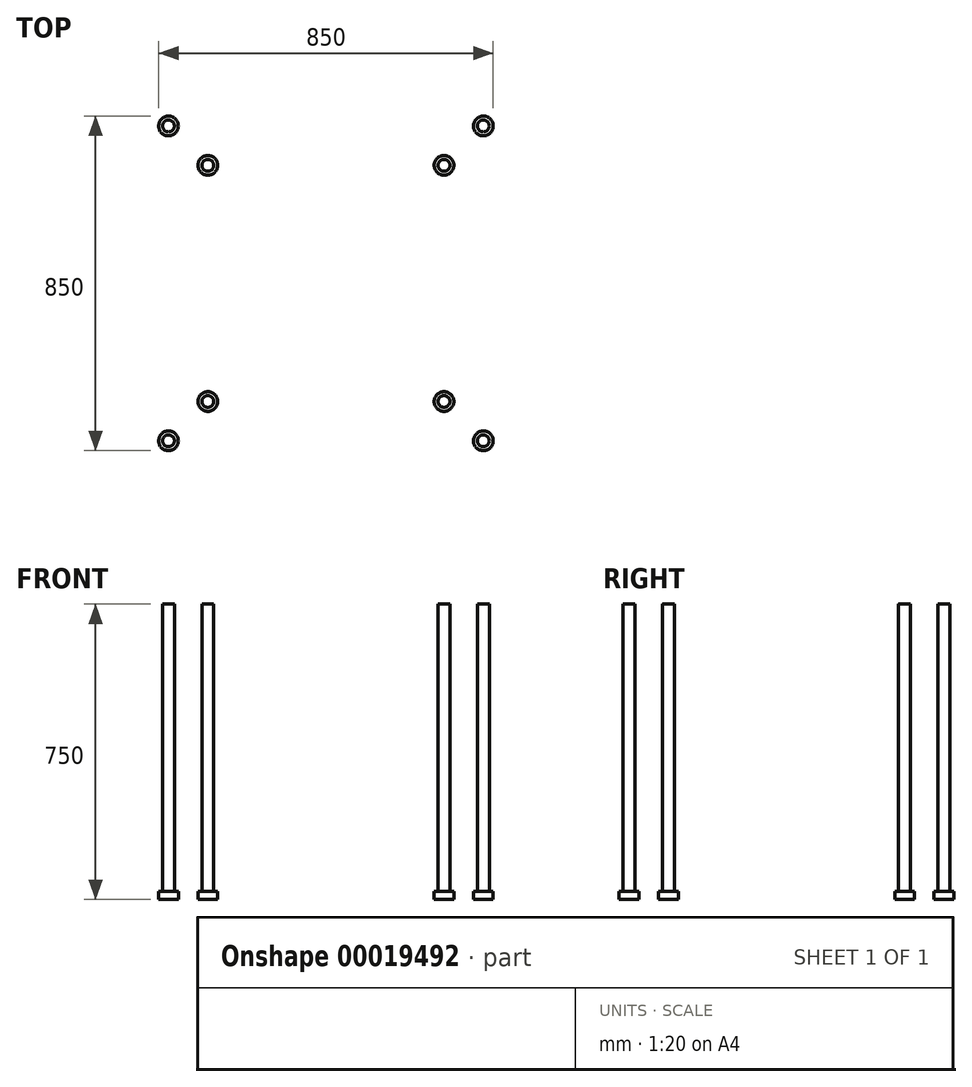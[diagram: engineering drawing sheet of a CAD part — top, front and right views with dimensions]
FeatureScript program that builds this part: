
annotation { "Feature Type Name" : "Feature", "Feature Type Description" : "" }
export const myFeature = defineFeature(function(context is Context, id is Id, definition is map)
    precondition{}
    {
        {
            var Q0;
            Q0=qCreatedBy(makeId("Top.planeOp"),FACE);
            var sketch = newSketch(context, id + "F0", { "sketchPlane" : qUnion([Q0])});
            skLineSegment(sketch, "E0.rect.bottom", {"start": v(300, -300) * mm, "end": v(-300, -300) * mm});
            skLineSegment(sketch, "E0.rect.top", {"start": v(300, 300) * mm, "end": v(-300, 300) * mm});
            skLineSegment(sketch, "E0.rect.left", {"start": v(300, -300) * mm, "end": v(300, 300) * mm});
            skLineSegment(sketch, "E0.rect.right", {"start": v(-300, -300) * mm, "end": v(-300, 300) * mm});
            skPoint(sketch, "E0.rect.middle", {"position": v(0, 0) * mm});
            skLineSegment(sketch, "E1.rect.bottom", {"start": v(400, -400) * mm, "end": v(-400, -400) * mm});
            skLineSegment(sketch, "E1.rect.top", {"start": v(400, 400) * mm, "end": v(-400, 400) * mm});
            skLineSegment(sketch, "E1.rect.left", {"start": v(400, -400) * mm, "end": v(400, 400) * mm});
            skLineSegment(sketch, "E1.rect.right", {"start": v(-400, -400) * mm, "end": v(-400, 400) * mm});
            skCircle(sketch, "E2", {"center": v(-400, -400) * mm, "radius": 25 * mm});
            skCircle(sketch, "E3", {"center": v(-300, -300) * mm, "radius": 25 * mm});
            skCircle(sketch, "E4", {"center": v(300, -300) * mm, "radius": 25 * mm});
            skCircle(sketch, "E5", {"center": v(400, -400) * mm, "radius": 25 * mm});
            skCircle(sketch, "E6", {"center": v(300, 300) * mm, "radius": 25 * mm});
            skCircle(sketch, "E7", {"center": v(400, 400) * mm, "radius": 25 * mm});
            skCircle(sketch, "E8", {"center": v(-400, 400) * mm, "radius": 25 * mm});
            skCircle(sketch, "E9", {"center": v(-300, 300) * mm, "radius": 25 * mm});
            skCircle(sketch, "E10", {"center": v(-400, 400) * mm, "radius": 15 * mm});
            skCircle(sketch, "E11", {"center": v(-300, 300) * mm, "radius": 15 * mm});
            skCircle(sketch, "E12", {"center": v(-400, -400) * mm, "radius": 15 * mm});
            skCircle(sketch, "E13", {"center": v(-300, -300) * mm, "radius": 15 * mm});
            skCircle(sketch, "E14", {"center": v(300, -300) * mm, "radius": 15 * mm});
            skCircle(sketch, "E15", {"center": v(400, -400) * mm, "radius": 15 * mm});
            skCircle(sketch, "E16", {"center": v(300, 300) * mm, "radius": 15 * mm});
            skCircle(sketch, "E17", {"center": v(400, 400) * mm, "radius": 15 * mm});
            skSolve(sketch);
        }
        {
            var Q0;
            {var subQ1=sQuery(id+"F0.wireOp",EDGE,"E1.rect.left");var subQ3=sQuery(id+"F0.wireOp",EDGE,"E1.rect.bottom");var subQ5=makeQuery(id+"F0.imprint","INTERSECT",VERTEX,{"derivedFrom":[subQ3,subQ1]});Q0=makeQuery(id+"F0.imprint","IMPRINT",FACE,{"disambiguationData":[TD([[makeQuery(id+"F0.imprint","IMPRINT",EDGE,{"disambiguationData":[TD([[subQ5,-1.0]])],"derivedFrom":subQ3}),1.0]])]});}
            var Q1;
            {var subQ1=sQuery(id+"F0.wireOp",EDGE,"E1.rect.left");var subQ3=sQuery(id+"F0.wireOp",EDGE,"E1.rect.bottom");var subQ5=makeQuery(id+"F0.imprint","INTERSECT",VERTEX,{"derivedFrom":[subQ3,subQ1]});Q1=makeQuery(id+"F0.imprint","IMPRINT",FACE,{"disambiguationData":[TD([[makeQuery(id+"F0.imprint","IMPRINT",EDGE,{"disambiguationData":[TD([[subQ5,-1.0]])],"derivedFrom":subQ3}),-1.0]])]});}
            var Q2;
            {var subQ1=sQuery(id+"F0.wireOp",EDGE,"E0.rect.left");var subQ3=sQuery(id+"F0.wireOp",EDGE,"E0.rect.bottom");var subQ5=makeQuery(id+"F0.imprint","INTERSECT",VERTEX,{"derivedFrom":[subQ3,subQ1]});Q2=makeQuery(id+"F0.imprint","IMPRINT",FACE,{"disambiguationData":[TD([[makeQuery(id+"F0.imprint","IMPRINT",EDGE,{"disambiguationData":[TD([[subQ5,-1.0]])],"derivedFrom":subQ3}),1.0]])]});}
            var Q3;
            {var subQ1=sQuery(id+"F0.wireOp",EDGE,"E0.rect.left");var subQ3=sQuery(id+"F0.wireOp",EDGE,"E0.rect.bottom");var subQ5=makeQuery(id+"F0.imprint","INTERSECT",VERTEX,{"derivedFrom":[subQ3,subQ1]});Q3=makeQuery(id+"F0.imprint","IMPRINT",FACE,{"disambiguationData":[TD([[makeQuery(id+"F0.imprint","IMPRINT",EDGE,{"disambiguationData":[TD([[subQ5,-1.0]])],"derivedFrom":subQ3}),-1.0]])]});}
            var Q4;
            {var subQ1=sQuery(id+"F0.wireOp",EDGE,"E1.rect.left");var subQ3=sQuery(id+"F0.wireOp",EDGE,"E1.rect.top");var subQ5=makeQuery(id+"F0.imprint","INTERSECT",VERTEX,{"derivedFrom":[subQ3,subQ1]});Q4=makeQuery(id+"F0.imprint","IMPRINT",FACE,{"disambiguationData":[TD([[makeQuery(id+"F0.imprint","IMPRINT",EDGE,{"disambiguationData":[TD([[subQ5,-1.0]])],"derivedFrom":subQ3}),1.0]])]});}
            var Q5;
            {var subQ1=sQuery(id+"F0.wireOp",EDGE,"E0.rect.left");var subQ3=sQuery(id+"F0.wireOp",EDGE,"E0.rect.top");var subQ5=makeQuery(id+"F0.imprint","INTERSECT",VERTEX,{"derivedFrom":[subQ3,subQ1]});Q5=makeQuery(id+"F0.imprint","IMPRINT",FACE,{"disambiguationData":[TD([[makeQuery(id+"F0.imprint","IMPRINT",EDGE,{"disambiguationData":[TD([[subQ5,-1.0]])],"derivedFrom":subQ3}),1.0]])]});}
            var Q6;
            {var subQ1=sQuery(id+"F0.wireOp",EDGE,"E0.rect.left");var subQ3=sQuery(id+"F0.wireOp",EDGE,"E0.rect.top");var subQ5=makeQuery(id+"F0.imprint","INTERSECT",VERTEX,{"derivedFrom":[subQ3,subQ1]});Q6=makeQuery(id+"F0.imprint","IMPRINT",FACE,{"disambiguationData":[TD([[makeQuery(id+"F0.imprint","IMPRINT",EDGE,{"disambiguationData":[TD([[subQ5,-1.0]])],"derivedFrom":subQ3}),-1.0]])]});}
            var Q7;
            {var subQ1=sQuery(id+"F0.wireOp",EDGE,"E1.rect.left");var subQ3=sQuery(id+"F0.wireOp",EDGE,"E1.rect.top");var subQ5=makeQuery(id+"F0.imprint","INTERSECT",VERTEX,{"derivedFrom":[subQ3,subQ1]});Q7=makeQuery(id+"F0.imprint","IMPRINT",FACE,{"disambiguationData":[TD([[makeQuery(id+"F0.imprint","IMPRINT",EDGE,{"disambiguationData":[TD([[subQ5,-1.0]])],"derivedFrom":subQ3}),-1.0]])]});}
            var Q8;
            {var subQ1=sQuery(id+"F0.wireOp",EDGE,"E1.rect.right");var subQ3=sQuery(id+"F0.wireOp",EDGE,"E1.rect.bottom");var subQ5=makeQuery(id+"F0.imprint","INTERSECT",VERTEX,{"derivedFrom":[subQ3,subQ1]});Q8=makeQuery(id+"F0.imprint","IMPRINT",FACE,{"disambiguationData":[TD([[makeQuery(id+"F0.imprint","IMPRINT",EDGE,{"disambiguationData":[TD([[subQ5,1.0]])],"derivedFrom":subQ3}),1.0]])]});}
            var Q9;
            {var subQ1=sQuery(id+"F0.wireOp",EDGE,"E1.rect.right");var subQ3=sQuery(id+"F0.wireOp",EDGE,"E1.rect.bottom");var subQ5=makeQuery(id+"F0.imprint","INTERSECT",VERTEX,{"derivedFrom":[subQ3,subQ1]});Q9=makeQuery(id+"F0.imprint","IMPRINT",FACE,{"disambiguationData":[TD([[makeQuery(id+"F0.imprint","IMPRINT",EDGE,{"disambiguationData":[TD([[subQ5,1.0]])],"derivedFrom":subQ3}),-1.0]])]});}
            var Q10;
            {var subQ1=sQuery(id+"F0.wireOp",EDGE,"E0.rect.right");var subQ3=sQuery(id+"F0.wireOp",EDGE,"E0.rect.bottom");var subQ5=makeQuery(id+"F0.imprint","INTERSECT",VERTEX,{"derivedFrom":[subQ3,subQ1]});Q10=makeQuery(id+"F0.imprint","IMPRINT",FACE,{"disambiguationData":[TD([[makeQuery(id+"F0.imprint","IMPRINT",EDGE,{"disambiguationData":[TD([[subQ5,1.0]])],"derivedFrom":subQ3}),1.0]])]});}
            var Q11;
            {var subQ1=sQuery(id+"F0.wireOp",EDGE,"E0.rect.right");var subQ3=sQuery(id+"F0.wireOp",EDGE,"E0.rect.bottom");var subQ5=makeQuery(id+"F0.imprint","INTERSECT",VERTEX,{"derivedFrom":[subQ3,subQ1]});Q11=makeQuery(id+"F0.imprint","IMPRINT",FACE,{"disambiguationData":[TD([[makeQuery(id+"F0.imprint","IMPRINT",EDGE,{"disambiguationData":[TD([[subQ5,1.0]])],"derivedFrom":subQ3}),-1.0]])]});}
            var Q12;
            {var subQ1=sQuery(id+"F0.wireOp",EDGE,"E1.rect.right");var subQ3=sQuery(id+"F0.wireOp",EDGE,"E1.rect.top");var subQ5=makeQuery(id+"F0.imprint","INTERSECT",VERTEX,{"derivedFrom":[subQ3,subQ1]});Q12=makeQuery(id+"F0.imprint","IMPRINT",FACE,{"disambiguationData":[TD([[makeQuery(id+"F0.imprint","IMPRINT",EDGE,{"disambiguationData":[TD([[subQ5,1.0]])],"derivedFrom":subQ3}),-1.0]])]});}
            var Q13;
            {var subQ1=sQuery(id+"F0.wireOp",EDGE,"E1.rect.right");var subQ3=sQuery(id+"F0.wireOp",EDGE,"E1.rect.top");var subQ5=makeQuery(id+"F0.imprint","INTERSECT",VERTEX,{"derivedFrom":[subQ3,subQ1]});Q13=makeQuery(id+"F0.imprint","IMPRINT",FACE,{"disambiguationData":[TD([[makeQuery(id+"F0.imprint","IMPRINT",EDGE,{"disambiguationData":[TD([[subQ5,1.0]])],"derivedFrom":subQ3}),1.0]])]});}
            var Q14;
            {var subQ1=sQuery(id+"F0.wireOp",EDGE,"E0.rect.right");var subQ3=sQuery(id+"F0.wireOp",EDGE,"E0.rect.top");var subQ5=makeQuery(id+"F0.imprint","INTERSECT",VERTEX,{"derivedFrom":[subQ3,subQ1]});Q14=makeQuery(id+"F0.imprint","IMPRINT",FACE,{"disambiguationData":[TD([[makeQuery(id+"F0.imprint","IMPRINT",EDGE,{"disambiguationData":[TD([[subQ5,1.0]])],"derivedFrom":subQ3}),-1.0]])]});}
            var Q15;
            {var subQ1=sQuery(id+"F0.wireOp",EDGE,"E0.rect.right");var subQ3=sQuery(id+"F0.wireOp",EDGE,"E0.rect.top");var subQ5=makeQuery(id+"F0.imprint","INTERSECT",VERTEX,{"derivedFrom":[subQ3,subQ1]});Q15=makeQuery(id+"F0.imprint","IMPRINT",FACE,{"disambiguationData":[TD([[makeQuery(id+"F0.imprint","IMPRINT",EDGE,{"disambiguationData":[TD([[subQ5,1.0]])],"derivedFrom":subQ3}),1.0]])]});}
            extrude(context, id + "F1", {"entities" : qUnion([Q0, Q1, Q2, Q3, Q4, Q5, Q6, Q7, Q8, Q9, Q10, Q11, Q12, Q13, Q14, Q15]), "depth" : 750 * mm});
        }
        {
            var Q0;
            {var subQ3=sQuery(id+"F0.wireOp",EDGE,"E1.rect.bottom");var subQ5=sQuery(id+"F0.wireOp",EDGE,"E5");var subQ7=makeQuery(id+"F0.imprint","INTERSECT",VERTEX,{"derivedFrom":[subQ3,subQ5]});Q0=makeQuery(id+"F0.imprint","IMPRINT",FACE,{"disambiguationData":[TD([[makeQuery(id+"F0.imprint","IMPRINT",EDGE,{"disambiguationData":[TD([[subQ7,1.0]])],"derivedFrom":subQ3}),1.0]])]});}
            var Q1;
            {var subQ3=sQuery(id+"F0.wireOp",EDGE,"E1.rect.bottom");var subQ5=sQuery(id+"F0.wireOp",EDGE,"E5");var subQ7=makeQuery(id+"F0.imprint","INTERSECT",VERTEX,{"derivedFrom":[subQ3,subQ5]});Q1=makeQuery(id+"F0.imprint","IMPRINT",FACE,{"disambiguationData":[TD([[makeQuery(id+"F0.imprint","IMPRINT",EDGE,{"disambiguationData":[TD([[subQ7,1.0]])],"derivedFrom":subQ3}),-1.0]])]});}
            var Q2;
            {var subQ3=sQuery(id+"F0.wireOp",EDGE,"E1.rect.top");var subQ5=sQuery(id+"F0.wireOp",EDGE,"E7");var subQ7=makeQuery(id+"F0.imprint","INTERSECT",VERTEX,{"derivedFrom":[subQ3,subQ5]});Q2=makeQuery(id+"F0.imprint","IMPRINT",FACE,{"disambiguationData":[TD([[makeQuery(id+"F0.imprint","IMPRINT",EDGE,{"disambiguationData":[TD([[subQ7,1.0]])],"derivedFrom":subQ3}),-1.0]])]});}
            var Q3;
            {var subQ3=sQuery(id+"F0.wireOp",EDGE,"E1.rect.top");var subQ5=sQuery(id+"F0.wireOp",EDGE,"E7");var subQ7=makeQuery(id+"F0.imprint","INTERSECT",VERTEX,{"derivedFrom":[subQ3,subQ5]});Q3=makeQuery(id+"F0.imprint","IMPRINT",FACE,{"disambiguationData":[TD([[makeQuery(id+"F0.imprint","IMPRINT",EDGE,{"disambiguationData":[TD([[subQ7,1.0]])],"derivedFrom":subQ3}),1.0]])]});}
            var Q4;
            {var subQ0=sQuery(id+"F0.wireOp",EDGE,"E16");var subQ3=sQuery(id+"F0.wireOp",EDGE,"E0.rect.top");var subQ4=makeQuery(id+"F0.imprint","INTERSECT",VERTEX,{"derivedFrom":[subQ3,subQ0]});Q4=makeQuery(id+"F0.imprint","IMPRINT",FACE,{"disambiguationData":[TD([[makeQuery(id+"F0.imprint","IMPRINT",EDGE,{"disambiguationData":[TD([[subQ4,-1.0]])],"derivedFrom":subQ3}),1.0]])]});}
            var Q5;
            {var subQ0=sQuery(id+"F0.wireOp",EDGE,"E16");var subQ3=sQuery(id+"F0.wireOp",EDGE,"E0.rect.top");var subQ4=makeQuery(id+"F0.imprint","INTERSECT",VERTEX,{"derivedFrom":[subQ3,subQ0]});Q5=makeQuery(id+"F0.imprint","IMPRINT",FACE,{"disambiguationData":[TD([[makeQuery(id+"F0.imprint","IMPRINT",EDGE,{"disambiguationData":[TD([[subQ4,-1.0]])],"derivedFrom":subQ3}),-1.0]])]});}
            var Q6;
            {var subQ3=sQuery(id+"F0.wireOp",EDGE,"E0.rect.top");var subQ5=sQuery(id+"F0.wireOp",EDGE,"E9");var subQ7=makeQuery(id+"F0.imprint","INTERSECT",VERTEX,{"derivedFrom":[subQ3,subQ5]});Q6=makeQuery(id+"F0.imprint","IMPRINT",FACE,{"disambiguationData":[TD([[makeQuery(id+"F0.imprint","IMPRINT",EDGE,{"disambiguationData":[TD([[subQ7,-1.0]])],"derivedFrom":subQ3}),1.0]])]});}
            var Q7;
            {var subQ3=sQuery(id+"F0.wireOp",EDGE,"E0.rect.top");var subQ5=sQuery(id+"F0.wireOp",EDGE,"E9");var subQ7=makeQuery(id+"F0.imprint","INTERSECT",VERTEX,{"derivedFrom":[subQ3,subQ5]});Q7=makeQuery(id+"F0.imprint","IMPRINT",FACE,{"disambiguationData":[TD([[makeQuery(id+"F0.imprint","IMPRINT",EDGE,{"disambiguationData":[TD([[subQ7,-1.0]])],"derivedFrom":subQ3}),-1.0]])]});}
            var Q8;
            {var subQ3=sQuery(id+"F0.wireOp",EDGE,"E1.rect.top");var subQ5=sQuery(id+"F0.wireOp",EDGE,"E8");var subQ7=makeQuery(id+"F0.imprint","INTERSECT",VERTEX,{"derivedFrom":[subQ3,subQ5]});Q8=makeQuery(id+"F0.imprint","IMPRINT",FACE,{"disambiguationData":[TD([[makeQuery(id+"F0.imprint","IMPRINT",EDGE,{"disambiguationData":[TD([[subQ7,-1.0]])],"derivedFrom":subQ3}),1.0]])]});}
            var Q9;
            {var subQ3=sQuery(id+"F0.wireOp",EDGE,"E1.rect.top");var subQ5=sQuery(id+"F0.wireOp",EDGE,"E8");var subQ7=makeQuery(id+"F0.imprint","INTERSECT",VERTEX,{"derivedFrom":[subQ3,subQ5]});Q9=makeQuery(id+"F0.imprint","IMPRINT",FACE,{"disambiguationData":[TD([[makeQuery(id+"F0.imprint","IMPRINT",EDGE,{"disambiguationData":[TD([[subQ7,-1.0]])],"derivedFrom":subQ3}),-1.0]])]});}
            var Q10;
            {var subQ3=sQuery(id+"F0.wireOp",EDGE,"E1.rect.bottom");var subQ5=sQuery(id+"F0.wireOp",EDGE,"E2");var subQ7=makeQuery(id+"F0.imprint","INTERSECT",VERTEX,{"derivedFrom":[subQ3,subQ5]});Q10=makeQuery(id+"F0.imprint","IMPRINT",FACE,{"disambiguationData":[TD([[makeQuery(id+"F0.imprint","IMPRINT",EDGE,{"disambiguationData":[TD([[subQ7,-1.0]])],"derivedFrom":subQ3}),-1.0]])]});}
            var Q11;
            {var subQ3=sQuery(id+"F0.wireOp",EDGE,"E0.rect.bottom");var subQ5=sQuery(id+"F0.wireOp",EDGE,"E3");var subQ7=makeQuery(id+"F0.imprint","INTERSECT",VERTEX,{"derivedFrom":[subQ3,subQ5]});Q11=makeQuery(id+"F0.imprint","IMPRINT",FACE,{"disambiguationData":[TD([[makeQuery(id+"F0.imprint","IMPRINT",EDGE,{"disambiguationData":[TD([[subQ7,-1.0]])],"derivedFrom":subQ3}),-1.0]])]});}
            var Q12;
            {var subQ3=sQuery(id+"F0.wireOp",EDGE,"E0.rect.bottom");var subQ5=sQuery(id+"F0.wireOp",EDGE,"E3");var subQ7=makeQuery(id+"F0.imprint","INTERSECT",VERTEX,{"derivedFrom":[subQ3,subQ5]});Q12=makeQuery(id+"F0.imprint","IMPRINT",FACE,{"disambiguationData":[TD([[makeQuery(id+"F0.imprint","IMPRINT",EDGE,{"disambiguationData":[TD([[subQ7,-1.0]])],"derivedFrom":subQ3}),1.0]])]});}
            var Q13;
            {var subQ3=sQuery(id+"F0.wireOp",EDGE,"E1.rect.bottom");var subQ5=sQuery(id+"F0.wireOp",EDGE,"E2");var subQ7=makeQuery(id+"F0.imprint","INTERSECT",VERTEX,{"derivedFrom":[subQ3,subQ5]});Q13=makeQuery(id+"F0.imprint","IMPRINT",FACE,{"disambiguationData":[TD([[makeQuery(id+"F0.imprint","IMPRINT",EDGE,{"disambiguationData":[TD([[subQ7,-1.0]])],"derivedFrom":subQ3}),1.0]])]});}
            var Q14;
            {var subQ0=sQuery(id+"F0.wireOp",EDGE,"E14");var subQ3=sQuery(id+"F0.wireOp",EDGE,"E0.rect.bottom");var subQ4=makeQuery(id+"F0.imprint","INTERSECT",VERTEX,{"derivedFrom":[subQ3,subQ0]});Q14=makeQuery(id+"F0.imprint","IMPRINT",FACE,{"disambiguationData":[TD([[makeQuery(id+"F0.imprint","IMPRINT",EDGE,{"disambiguationData":[TD([[subQ4,-1.0]])],"derivedFrom":subQ3}),1.0]])]});}
            var Q15;
            {var subQ0=sQuery(id+"F0.wireOp",EDGE,"E14");var subQ3=sQuery(id+"F0.wireOp",EDGE,"E0.rect.bottom");var subQ4=makeQuery(id+"F0.imprint","INTERSECT",VERTEX,{"derivedFrom":[subQ3,subQ0]});Q15=makeQuery(id+"F0.imprint","IMPRINT",FACE,{"disambiguationData":[TD([[makeQuery(id+"F0.imprint","IMPRINT",EDGE,{"disambiguationData":[TD([[subQ4,-1.0]])],"derivedFrom":subQ3}),-1.0]])]});}
            extrude(context, id + "F2", {"entities" : qUnion([Q0, Q1, Q2, Q3, Q4, Q5, Q6, Q7, Q8, Q9, Q10, Q11, Q12, Q13, Q14, Q15]), "operationType" : NewBodyOperationType.ADD, "depth" : 20 * mm});
        }
    });
